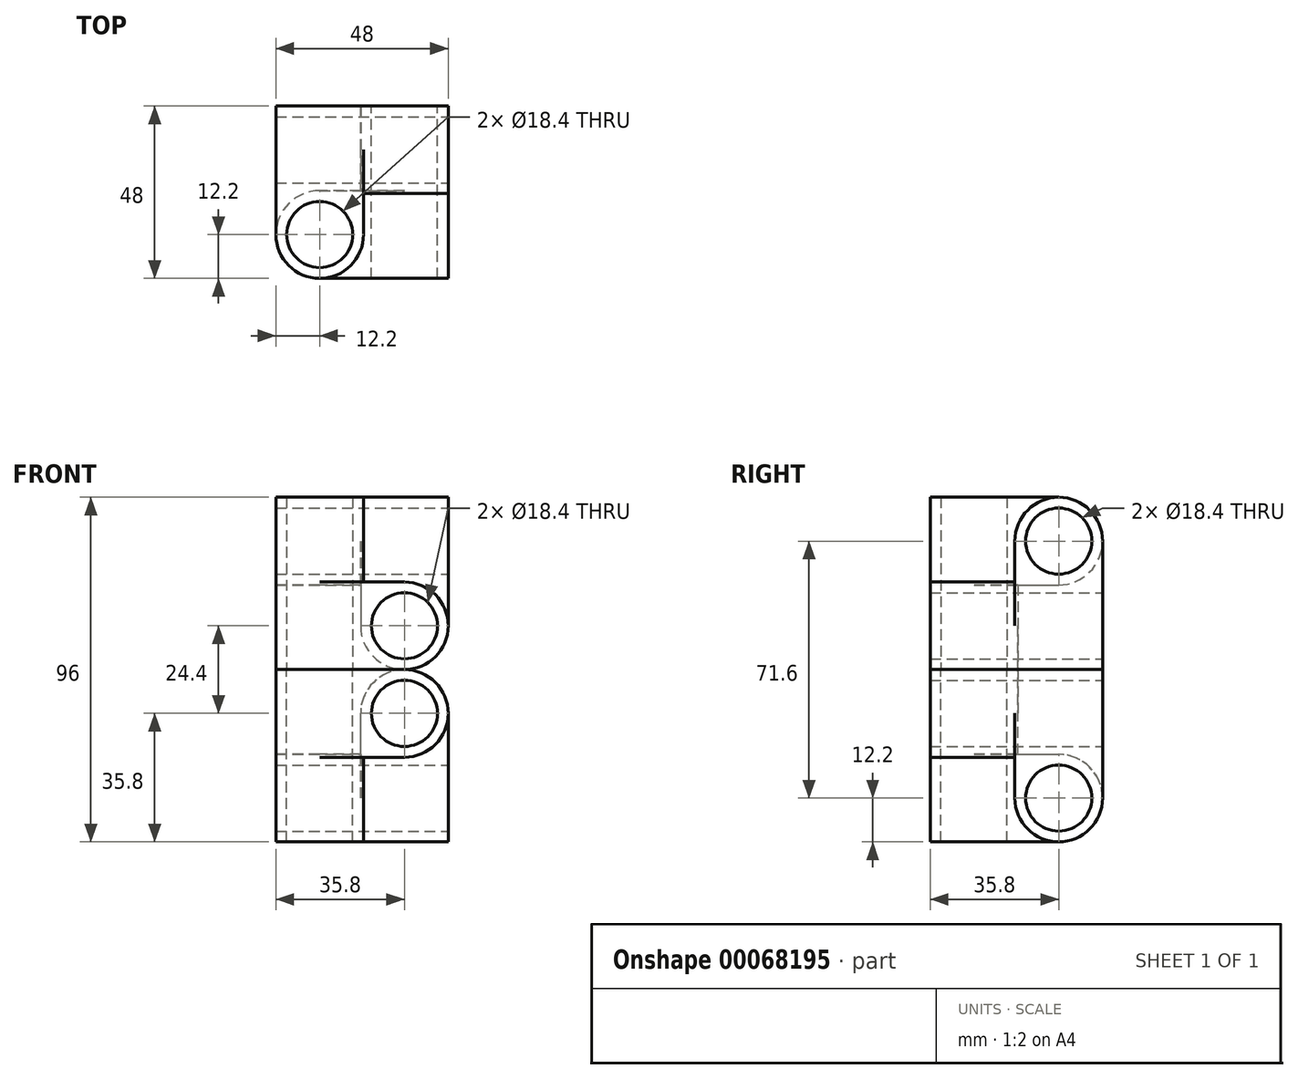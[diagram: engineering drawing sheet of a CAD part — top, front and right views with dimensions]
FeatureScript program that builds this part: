
annotation { "Feature Type Name" : "Feature", "Feature Type Description" : "" }
export const myFeature = defineFeature(function(context is Context, id is Id, definition is map)
    precondition{}
    {
        {
            var Q0;
            Q0=qCreatedBy(makeId("Front.planeOp"),FACE);
            var sketch = newSketch(context, id + "F0", { "sketchPlane" : qUnion([Q0])});
            skCircle(sketch, "E0", {"center": v(-12.2, 12.2) * mm, "radius": 12.2 * mm});
            skCircle(sketch, "E1", {"center": v(-12.2, 12.2) * mm, "radius": 9.2 * mm});
            skSolve(sketch);
        }
        {
            var Q0;
            Q0 = qSketchRegion(id + "F0", true);
            extrude(context, id + "F1", {"entities" : qUnion([Q0]), "depth" : 48 * mm});
        }
        {
            var Q0;
            Q0=qCreatedBy(makeId("Right.planeOp"),FACE);
            var sketch = newSketch(context, id + "F2", { "sketchPlane" : qUnion([Q0])});
            skCircle(sketch, "E2", {"center": v(-12.2, 35.8) * mm, "radius": 12.2 * mm});
            skCircle(sketch, "E3", {"center": v(-12.2, 35.8) * mm, "radius": 9.2 * mm});
            skSolve(sketch);
        }
        {
            var Q0;
            Q0 = qSketchRegion(id + "F2", true);
            extrude(context, id + "F3", {"entities" : qUnion([Q0]), "operationType" : NewBodyOperationType.ADD, "oppositeDirection" : true, "depth" : 48 * mm});
        }
        {
            var Q0;
            Q0=qCreatedBy(makeId("Top.planeOp"),FACE);
            var sketch = newSketch(context, id + "F4", { "sketchPlane" : qUnion([Q0])});
            skCircle(sketch, "E4", {"center": v(-35.8, -35.8) * mm, "radius": 12.2 * mm});
            skCircle(sketch, "E5", {"center": v(-35.8, -35.8) * mm, "radius": 9.2 * mm});
            skSolve(sketch);
        }
        {
            var Q0;
            Q0 = qSketchRegion(id + "F4", true);
            extrude(context, id + "F5", {"entities" : qUnion([Q0]), "operationType" : NewBodyOperationType.ADD, "depth" : 48 * mm});
        }
        {
            var Q0;
            Q0=qCreatedBy(makeId("Front.planeOp"),FACE);
            cPlane(context, id + "F6", {"entities" : qUnion([Q0]), "cplaneType" : CPlaneType.OFFSET, "offset" : (24.4 / 2) * mm, "width" : 150 * mm, "height" : 150 * mm});
        }
        {
            var Q0;
            Q0=qCreatedBy(id+"F6.planeOp",FACE);
            var sketch = newSketch(context, id + "F7", { "sketchPlane" : qUnion([Q0])});
            skLineSegment(sketch, "E6.bottom", {"start": v(-48, 48) * mm, "end": v(-23.6, 48) * mm});
            skLineSegment(sketch, "E6.top", {"start": v(-48, 23.6) * mm, "end": v(-23.6, 23.6) * mm});
            skLineSegment(sketch, "E6.left", {"start": v(-48, 48) * mm, "end": v(-48, 23.6) * mm});
            skLineSegment(sketch, "E6.right", {"start": v(-23.6, 48) * mm, "end": v(-23.6, 23.6) * mm});
            skSolve(sketch);
        }
        {
            var Q0;
            Q0 = qSketchRegion(id + "F7", true);
            var Q1;
            Q1=makeQuery(id+"F5.opExtrude","SWEPT_FACE",FACE,{"disambiguationData":[OSD([sQuery(id+"F4.wireOp",EDGE,"E4")])]});
            extrude(context, id + "F8", {"entities" : qUnion([Q0]), "operationType" : NewBodyOperationType.ADD, "endBound" : BoundingType.UP_TO_SURFACE, "endBoundEntityFace" : qUnion([Q1]), "depth" : 25 * mm});
        }
        {
            var Q0;
            Q0=qCreatedBy(makeId("Right.planeOp"),FACE);
            cPlane(context, id + "F9", {"entities" : qUnion([Q0]), "cplaneType" : CPlaneType.OFFSET, "offset" : (24.4 / 2) * mm, "oppositeDirection" : true, "width" : 150 * mm, "height" : 150 * mm});
        }
        {
            var Q0;
            Q0=qCreatedBy(id+"F9.planeOp",FACE);
            var sketch = newSketch(context, id + "F10", { "sketchPlane" : qUnion([Q0])});
            skLineSegment(sketch, "E7.bottom", {"start": v(-48, 0) * mm, "end": v(-23.6, 0) * mm});
            skLineSegment(sketch, "E7.top", {"start": v(-48, 24.4) * mm, "end": v(-23.6, 24.4) * mm});
            skLineSegment(sketch, "E7.left", {"start": v(-48, 0) * mm, "end": v(-48, 24.4) * mm});
            skLineSegment(sketch, "E7.right", {"start": v(-23.6, 0) * mm, "end": v(-23.6, 24.4) * mm});
            skSolve(sketch);
        }
        {
            var Q0;
            Q0 = qSketchRegion(id + "F10", true);
            var Q1;
            Q1=makeQuery(id+"F5.opExtrude","SWEPT_FACE",FACE,{"disambiguationData":[OSD([sQuery(id+"F4.wireOp",EDGE,"E4")])]});
            extrude(context, id + "F11", {"entities" : qUnion([Q0]), "operationType" : NewBodyOperationType.ADD, "endBound" : BoundingType.UP_TO_SURFACE, "oppositeDirection" : true, "endBoundEntityFace" : qUnion([Q1]), "depth" : 25 * mm});
        }
        {
            var Q0;
            Q0=qCreatedBy(makeId("Top.planeOp"),FACE);
            cPlane(context, id + "F12", {"entities" : qUnion([Q0]), "cplaneType" : CPlaneType.OFFSET, "offset" : (24.4 / 2) * mm, "width" : 150 * mm, "height" : 150 * mm});
        }
        {
            var Q0;
            Q0=qCreatedBy(id+"F12.planeOp",FACE);
            var sketch = newSketch(context, id + "F13", { "sketchPlane" : qUnion([Q0])});
            skLineSegment(sketch, "E8.bottom", {"start": v(0, 0) * mm, "end": v(-24.4, 0) * mm});
            skLineSegment(sketch, "E8.top", {"start": v(0, -24.4) * mm, "end": v(-24.4, -24.4) * mm});
            skLineSegment(sketch, "E8.left", {"start": v(0, 0) * mm, "end": v(0, -24.4) * mm});
            skLineSegment(sketch, "E8.right", {"start": v(-24.4, 0) * mm, "end": v(-24.4, -24.4) * mm});
            skSolve(sketch);
        }
        {
            var Q0;
            Q0 = qSketchRegion(id + "F13", true);
            var Q1;
            Q1=makeQuery(id+"F3.opExtrude","SWEPT_FACE",FACE,{"disambiguationData":[OSD([sQuery(id+"F2.wireOp",EDGE,"E2")])]});
            extrude(context, id + "F14", {"entities" : qUnion([Q0]), "operationType" : NewBodyOperationType.ADD, "endBound" : BoundingType.UP_TO_SURFACE, "endBoundEntityFace" : qUnion([Q1]), "depth" : 25 * mm});
        }
        {
            var Q0;
            Q0=makeQuery(id+"F11.boolean.opBoolean","MERGE",FACE,{"derivedFrom":[makeQuery(id+"F1.opExtrude","CAP_FACE",FACE,{"disambiguationData":[OSD([sQuery(id+"F0.wireOp",EDGE,"E0"),sQuery(id+"F0.wireOp",EDGE,"E1")])],"isStart":false}),makeQuery(id+"F11.opExtrude","SWEPT_FACE",FACE,{"disambiguationData":[OSD([sQuery(id+"F10.wireOp",EDGE,"E7.left")])]})]});
            var sketch = newSketch(context, id + "F15", { "sketchPlane" : qUnion([Q0])});
            skCircle(sketch, "E9", {"center": v(-12.2, 12.2) * mm, "radius": 9.2 * mm});
            skSolve(sketch);
        }
        {
            var Q0;
            Q0 = qSketchRegion(id + "F15", true);
            extrude(context, id + "F16", {"entities" : qUnion([Q0]), "operationType" : NewBodyOperationType.REMOVE, "endBound" : BoundingType.THROUGH_ALL, "oppositeDirection" : true, "depth" : 25 * mm});
        }
        {
            var Q0;
            Q0=makeQuery(id+"F8.boolean.opBoolean","MERGE",FACE,{"derivedFrom":[makeQuery(id+"F3.opExtrude","CAP_FACE",FACE,{"disambiguationData":[OSD([sQuery(id+"F2.wireOp",EDGE,"E2"),sQuery(id+"F2.wireOp",EDGE,"E3")])],"isStart":false}),makeQuery(id+"F8.opExtrude","SWEPT_FACE",FACE,{"disambiguationData":[OSD([sQuery(id+"F7.wireOp",EDGE,"E6.left")])]})]});
            var sketch = newSketch(context, id + "F17", { "sketchPlane" : qUnion([Q0])});
            skCircle(sketch, "E10", {"center": v(12.2, 35.8) * mm, "radius": 9.2 * mm});
            skSolve(sketch);
        }
        {
            var Q0;
            Q0 = qSketchRegion(id + "F17", true);
            extrude(context, id + "F18", {"entities" : qUnion([Q0]), "operationType" : NewBodyOperationType.REMOVE, "endBound" : BoundingType.THROUGH_ALL, "oppositeDirection" : true, "depth" : 25 * mm});
        }
        {
            var Q0;
            Q0=makeQuery(id+"F1.opExtrude","SWEPT_BODY",BODY,{"disambiguationData":[OSD([sQuery(id+"F0.wireOp",EDGE,"E0"),sQuery(id+"F0.wireOp",EDGE,"E1")])]});
            var Q1;
            Q1=qCreatedBy(makeId("Top.planeOp"),FACE);
            mirror(context, id + "F19", {"entities" : qUnion([Q0]), "mirrorPlane" : qUnion([Q1])});
        }
    });
